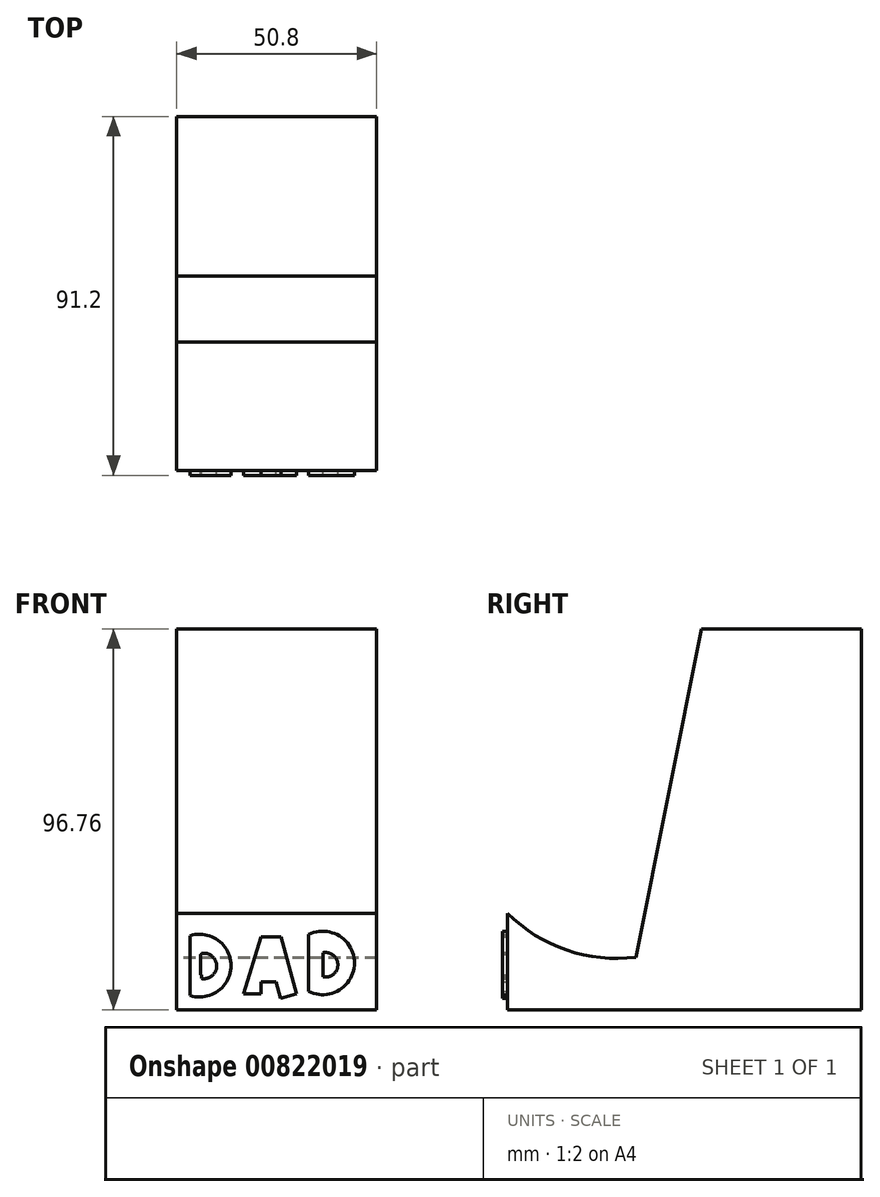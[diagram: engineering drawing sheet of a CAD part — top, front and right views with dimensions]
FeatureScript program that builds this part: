
annotation { "Feature Type Name" : "Feature", "Feature Type Description" : "" }
export const myFeature = defineFeature(function(context is Context, id is Id, definition is map)
    precondition{}
    {
        {
            var Q0;
            Q0=qCreatedBy(makeId("Right.planeOp"),FACE);
            var sketch = newSketch(context, id + "F0", { "sketchPlane" : qUnion([Q0])});
            skLineSegment(sketch, "E0", {"start": v(-8.22, -23.1) * mm, "end": v(8.53, 60.32) * mm});
            skLineSegment(sketch, "E1", {"start": v(8.53, 60.32) * mm, "end": v(49.15, 60.32) * mm});
            skLineSegment(sketch, "E2", {"start": v(49.15, 60.32) * mm, "end": v(49.15, -36.44) * mm});
            skLineSegment(sketch, "E3", {"start": v(49.15, -36.44) * mm, "end": v(-40.78, -36.44) * mm});
            skLineSegment(sketch, "E4", {"start": v(-40.78, -36.44) * mm, "end": v(-40.78, -11.94) * mm});
            skArc(sketch, "E5", {"start": v(-40.78, -11.94) * mm, "mid": v(-25.8, -21.31) * mm, "end": v(-8.22, -23.1) * mm});
            skSolve(sketch);
        }
        {
            var Q0;
            Q0=makeQuery(id+"F0.imprint","IMPRINT",FACE,{"disambiguationData":[TD([[makeQuery(id+"F0.imprint","IMPRINT",EDGE,{"derivedFrom":sQuery(id+"F0.wireOp",EDGE,"E0")}),-1.0]])]});
            extrude(context, id + "F1", {"entities" : qUnion([Q0]), "depth" : 50.8 * mm, "offsetDistance" : 25.4 * mm});
        }
        {
            var Q0;
            Q0=makeQuery(id+"F1.opExtrude","SWEPT_FACE",FACE,{"disambiguationData":[OSD([sQuery(id+"F0.wireOp",EDGE,"E4")])]});
            var sketch = newSketch(context, id + "F2", { "sketchPlane" : qUnion([Q0])});
            skLineSegment(sketch, "E6", {"start": v(3.42, -15.69) * mm, "end": v(3.42, -34.37) * mm});
            skArc(sketch, "E7", {"start": v(3.42, -34.37) * mm, "mid": v(15.64, -25.03) * mm, "end": v(3.42, -15.69) * mm});
            skSolve(sketch);
        }
        {
            var Q0;
            Q0=makeQuery(id+"F2.imprint","IMPRINT",FACE,{"disambiguationData":[TD([[makeQuery(id+"F2.imprint","IMPRINT",EDGE,{"derivedFrom":sQuery(id+"F2.wireOp",EDGE,"E6")}),-1.0]])]});
            var sketch = newSketch(context, id + "F3", { "sketchPlane" : qUnion([Q0])});
            skLineSegment(sketch, "E8", {"start": v(17.04, -32.4) * mm, "end": v(21.44, -17.89) * mm});
            skLineSegment(sketch, "E9", {"start": v(21.44, -17.89) * mm, "end": v(26.5, -17.89) * mm});
            skLineSegment(sketch, "E10", {"start": v(26.5, -17.89) * mm, "end": v(30.45, -32.4) * mm});
            skLineSegment(sketch, "E11", {"start": v(30.45, -32.4) * mm, "end": v(26.36, -33.5) * mm});
            skLineSegment(sketch, "E12", {"start": v(26.36, -33.5) * mm, "end": v(25.23, -29.34) * mm});
            skLineSegment(sketch, "E13", {"start": v(25.23, -29.34) * mm, "end": v(21.44, -29.34) * mm});
            skLineSegment(sketch, "E14", {"start": v(21.44, -29.34) * mm, "end": v(21.44, -32.4) * mm});
            skLineSegment(sketch, "E15", {"start": v(21.44, -32.4) * mm, "end": v(17.04, -32.4) * mm});
            skSolve(sketch);
        }
        {
            var Q0;
            Q0=makeQuery(id+"F2.imprint","IMPRINT",FACE,{"disambiguationData":[TD([[makeQuery(id+"F2.imprint","IMPRINT",EDGE,{"derivedFrom":sQuery(id+"F2.wireOp",EDGE,"E6")}),-1.0]])]});
            var sketch = newSketch(context, id + "F4", { "sketchPlane" : qUnion([Q0])});
            skLineSegment(sketch, "E16", {"start": v(23.72, -21.98) * mm, "end": v(22.05, -26.24) * mm});
            skLineSegment(sketch, "E17", {"start": v(22.05, -26.24) * mm, "end": v(24.83, -26.24) * mm});
            skLineSegment(sketch, "E18", {"start": v(24.83, -26.24) * mm, "end": v(23.72, -21.98) * mm});
            skLineSegment(sketch, "E19", {"start": v(33.52, -17.36) * mm, "end": v(33.52, -31.79) * mm});
            skArc(sketch, "E20", {"start": v(33.52, -31.79) * mm, "mid": v(45.16, -24.57) * mm, "end": v(33.52, -17.36) * mm});
            skLineSegment(sketch, "E21", {"start": v(37.22, -21.98) * mm, "end": v(37.22, -28.09) * mm});
            skArc(sketch, "E22", {"start": v(37.22, -28.09) * mm, "mid": v(40.96, -25.04) * mm, "end": v(37.22, -21.98) * mm});
            skSolve(sketch);
        }
        {
            var Q0;
            Q0=makeQuery(id+"F4.imprint","IMPRINT",FACE,{"disambiguationData":[TD([[makeQuery(id+"F4.imprint","IMPRINT",EDGE,{"derivedFrom":sQuery(id+"F4.wireOp",EDGE,"E19")}),1.0]])]});
            extrude(context, id + "F5", {"entities" : qUnion([Q0]), "operationType" : NewBodyOperationType.ADD, "depth" : 1.27 * mm, "offsetDistance" : 25.4 * mm});
        }
        {
            var Q0;
            Q0=makeQuery(id+"F3.imprint","IMPRINT",FACE,{"disambiguationData":[TD([[makeQuery(id+"F3.imprint","IMPRINT",EDGE,{"derivedFrom":sQuery(id+"F3.wireOp",EDGE,"E8")}),-1.0]])]});
            extrude(context, id + "F6", {"entities" : qUnion([Q0]), "operationType" : NewBodyOperationType.ADD, "depth" : 1.27 * mm, "offsetDistance" : 25.4 * mm});
        }
        {
            var Q0;
            {var subQ0=sQuery(id+"F0.wireOp",EDGE,"E3");var subQ2=sQuery(id+"F0.wireOp",EDGE,"E4");Q0=makeQuery(id+"F5.boolean.opBoolean","SPLIT",FACE,{"disambiguationData":[TD([makeQuery(id+"F1.opExtrude","SWEPT_FACE",FACE,{"disambiguationData":[OSD([subQ0])]})])],"derivedFrom":makeQuery(id+"F1.opExtrude","SWEPT_FACE",FACE,{"disambiguationData":[OSD([subQ2])]})});}
            var sketch = newSketch(context, id + "F7", { "sketchPlane" : qUnion([Q0])});
            skLineSegment(sketch, "E23", {"start": v(6.06, -22.41) * mm, "end": v(6.06, -27.57) * mm});
            skArc(sketch, "E24", {"start": v(6.06, -27.57) * mm, "mid": v(9.83, -25) * mm, "end": v(6.06, -22.41) * mm});
            skSolve(sketch);
        }
        {
            var Q0;
            Q0=makeQuery(id+"F7.imprint","IMPRINT",FACE,{"disambiguationData":[TD([[makeQuery(id+"F7.imprint","IMPRINT",EDGE,{"derivedFrom":sQuery(id+"F7.wireOp",EDGE,"E23")}),-1.0]])]});
            var sketch = newSketch(context, id + "F8", { "sketchPlane" : qUnion([Q0])});
            skLineSegment(sketch, "E25", {"start": v(3.46, -17.64) * mm, "end": v(3.46, -32.85) * mm});
            skArc(sketch, "E26", {"start": v(3.46, -32.85) * mm, "mid": v(13.81, -25.25) * mm, "end": v(3.46, -17.64) * mm});
            skLineSegment(sketch, "E27", {"start": v(6.28, -22.15) * mm, "end": v(6.28, -28.53) * mm});
            skArc(sketch, "E28", {"start": v(6.28, -28.53) * mm, "mid": v(10.16, -25.34) * mm, "end": v(6.28, -22.15) * mm});
            skSolve(sketch);
        }
        {
            var Q0;
            Q0=makeQuery(id+"F8.imprint","IMPRINT",FACE,{"disambiguationData":[TD([[makeQuery(id+"F8.imprint","IMPRINT",EDGE,{"derivedFrom":sQuery(id+"F8.wireOp",EDGE,"E25")}),1.0]])]});
            extrude(context, id + "F9", {"entities" : qUnion([Q0]), "operationType" : NewBodyOperationType.ADD, "depth" : 1.27 * mm, "offsetDistance" : 25.4 * mm});
        }
    });
